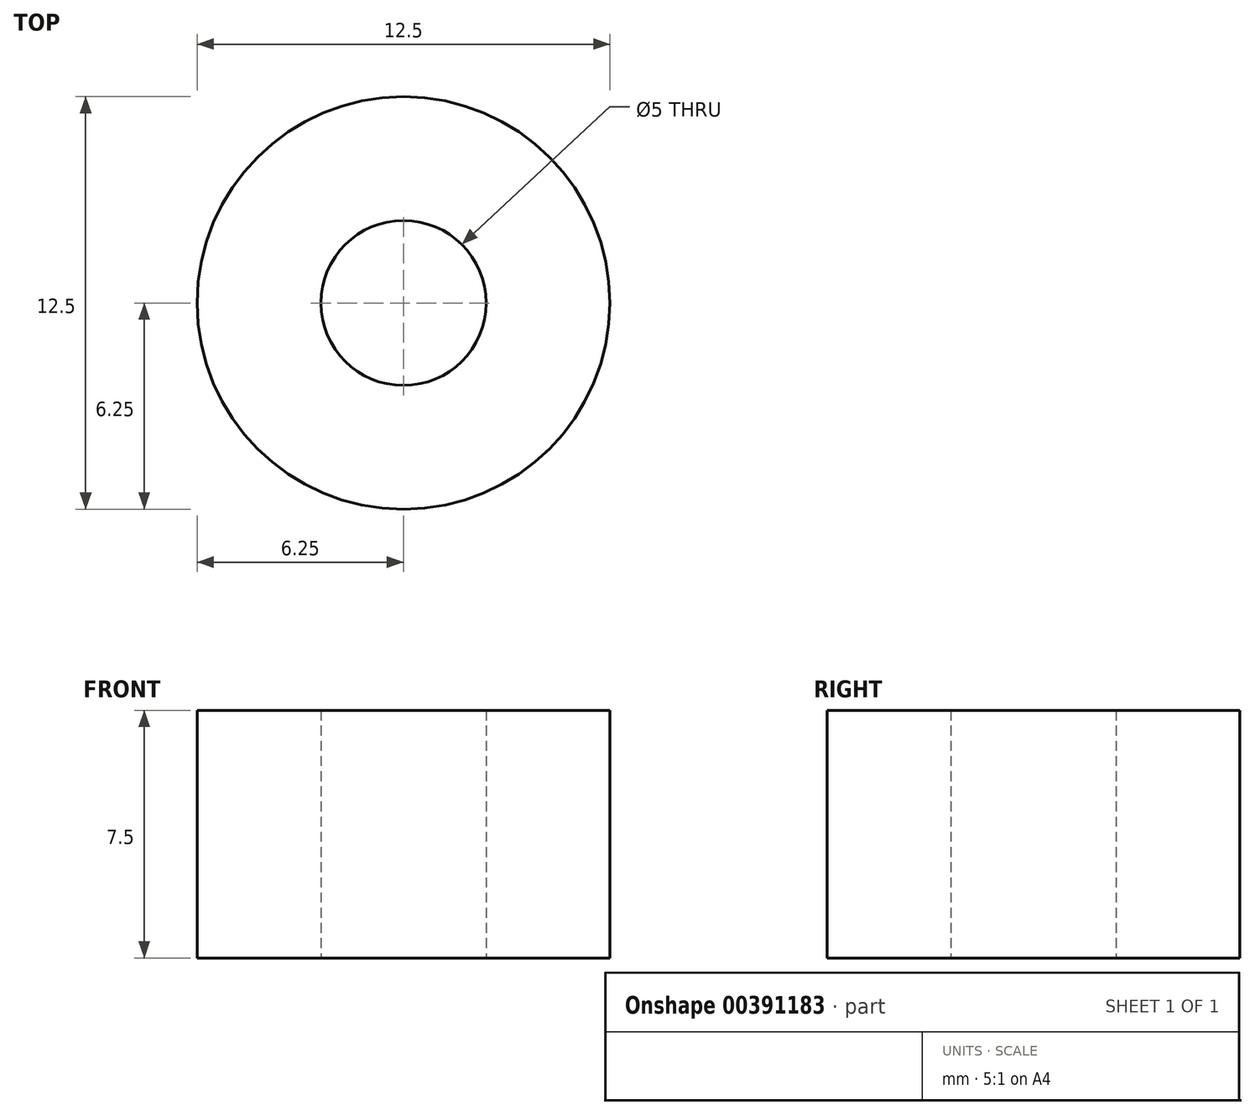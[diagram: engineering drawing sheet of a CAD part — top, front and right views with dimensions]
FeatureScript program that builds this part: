
annotation { "Feature Type Name" : "Feature", "Feature Type Description" : "" }
export const myFeature = defineFeature(function(context is Context, id is Id, definition is map)
    precondition{}
    {
        {
            var Q0;
            Q0=qCreatedBy(makeId("Top.planeOp"),FACE);
            var sketch = newSketch(context, id + "F0", { "sketchPlane" : qUnion([Q0])});
            skCircle(sketch, "E0", {"center": v(0, 0) * mm, "radius": 6.25 * mm});
            skCircle(sketch, "E1", {"center": v(0, 0) * mm, "radius": 2.5 * mm});
            skSolve(sketch);
        }
        {
            var Q0;
            Q0=makeQuery(id+"F0.imprint","IMPRINT",FACE,{"disambiguationData":[TD([[makeQuery(id+"F0.imprint","IMPRINT",EDGE,{"derivedFrom":sQuery(id+"F0.wireOp",EDGE,"E0")}),1.0]])]});
            extrude(context, id + "F1", {"entities" : qUnion([Q0]), "depth" : 7.5 * mm});
        }
    });
